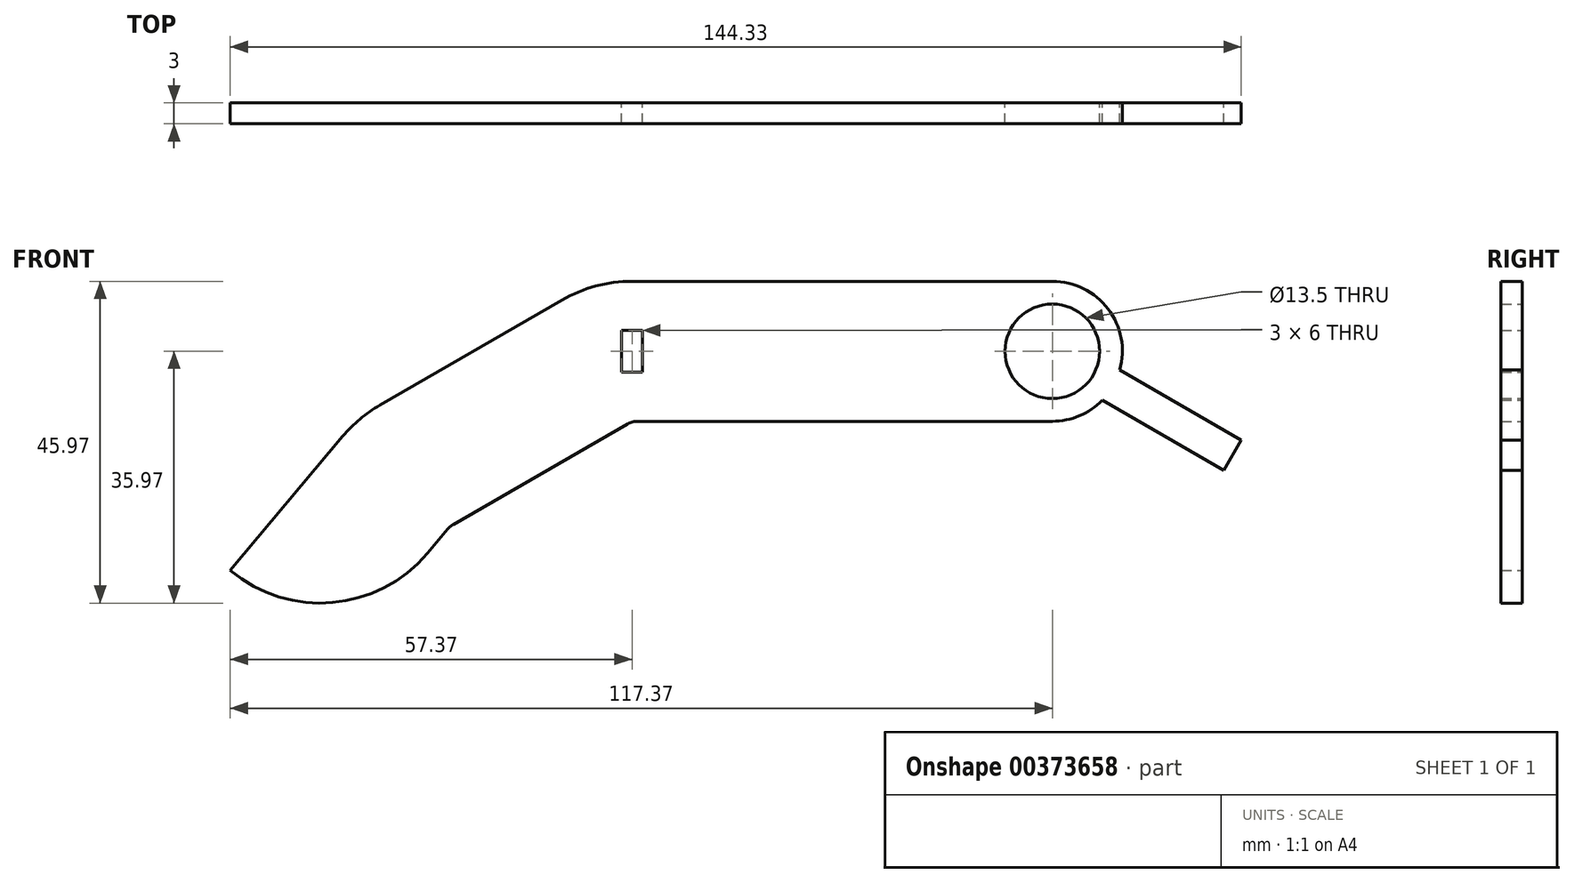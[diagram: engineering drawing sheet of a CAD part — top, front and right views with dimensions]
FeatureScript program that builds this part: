
annotation { "Feature Type Name" : "Feature", "Feature Type Description" : "" }
export const myFeature = defineFeature(function(context is Context, id is Id, definition is map)
    precondition{}
    {
        {
            var Q0;
            Q0=qCreatedBy(makeId("Front.planeOp"),FACE);
            var sketch = newSketch(context, id + "F0", { "sketchPlane" : qUnion([Q0])});
            skLineSegment(sketch, "E0.bottom", {"start": v(30, -10) * mm, "end": v(-30, -10) * mm});
            skLineSegment(sketch, "E0.top", {"start": v(30, 10) * mm, "end": v(-30, 10) * mm});
            skLineSegment(sketch, "E0.left", {"start": v(30, -10) * mm, "end": v(30, 10) * mm, "construction": true});
            skLineSegment(sketch, "E0.right", {"start": v(-30, -10) * mm, "end": v(-30, 10) * mm, "construction": true});
            skPoint(sketch, "E0.middle", {"position": v(0, 0) * mm});
            skArc(sketch, "E1", {"start": v(-30, 10) * mm, "mid": v(-35.18, 9.32) * mm, "end": v(-40, 7.32) * mm});
            skLineSegment(sketch, "E2", {"start": v(-40, 7.32) * mm, "end": v(-30, -10) * mm, "construction": true});
            skLineSegment(sketch, "E3", {"start": v(-40, 7.32) * mm, "end": v(-65.98, -7.68) * mm});
            skLineSegment(sketch, "E4", {"start": v(-30, -10) * mm, "end": v(-55.98, -25) * mm});
            skLineSegment(sketch, "E5", {"start": v(-65.98, -7.68) * mm, "end": v(-55.98, -25) * mm, "construction": true});
            skArc(sketch, "E6", {"start": v(-65.98, -7.68) * mm, "mid": v(-68.84, -9.68) * mm, "end": v(-71.3, -12.14) * mm});
            skLineSegment(sketch, "E7", {"start": v(-71.3, -12.14) * mm, "end": v(-55.98, -25) * mm, "construction": true});
            skLineSegment(sketch, "E8", {"start": v(-71.3, -12.14) * mm, "end": v(-87.37, -31.3) * mm});
            skLineSegment(sketch, "E9", {"start": v(-55.98, -25) * mm, "end": v(-59.2, -28.83) * mm});
            skArc(sketch, "E10", {"start": v(-87.37, -31.3) * mm, "mid": v(-72.77, -35.9) * mm, "end": v(-59.2, -28.83) * mm});
            skCircle(sketch, "E11", {"center": v(30, 0) * mm, "radius": 6.75 * mm});
            skLineSegment(sketch, "E12", {"start": v(30, 0) * mm, "end": v(55.7, -14.84) * mm, "construction": true});
            skArc(sketch, "E13", {"start": v(30, -10) * mm, "mid": v(33.87, -9.22) * mm, "end": v(37.14, -7) * mm});
            skArc(sketch, "E14", {"start": v(30, 10) * mm, "mid": v(37.96, 6.05) * mm, "end": v(39.64, -2.68) * mm});
            skLineSegment(sketch, "E15", {"start": v(56.96, -12.68) * mm, "end": v(54.46, -17) * mm});
            skLineSegment(sketch, "E16", {"start": v(54.46, -17) * mm, "end": v(37.14, -7) * mm});
            skLineSegment(sketch, "E17", {"start": v(56.96, -12.68) * mm, "end": v(39.64, -2.68) * mm});
            skLineSegment(sketch, "E18.bottom", {"start": v(-28.5, -3) * mm, "end": v(-31.5, -3) * mm});
            skLineSegment(sketch, "E18.top", {"start": v(-28.5, 3) * mm, "end": v(-31.5, 3) * mm});
            skLineSegment(sketch, "E18.left", {"start": v(-28.5, -3) * mm, "end": v(-28.5, 3) * mm});
            skLineSegment(sketch, "E18.right", {"start": v(-31.5, -3) * mm, "end": v(-31.5, 3) * mm});
            skPoint(sketch, "E18.middle", {"position": v(-30, 0) * mm});
            skSolve(sketch);
        }
        {
            var Q0;
            Q0 = qSketchRegion(id + "F0", true);
            extrude(context, id + "F1", {"entities" : qUnion([Q0]), "depth" : 3 * mm});
        }
        {
            var Q0;
            Q0=makeQuery(id+"F1.opExtrude","SWEPT_EDGE",EDGE,{"disambiguationData":[OSD([sQuery(id+"F0.wireOp",EDGE,"E0.bottom"),sQuery(id+"F0.wireOp",EDGE,"E4")])]});
            var Q1;
            Q1=makeQuery(id+"F1.opExtrude","SWEPT_EDGE",EDGE,{"disambiguationData":[OSD([sQuery(id+"F0.wireOp",EDGE,"E4"),sQuery(id+"F0.wireOp",EDGE,"E9")])]});
            fillet(context, id + "F2", {"entities" : qUnion([Q0, Q1]), "radius" : 3 * mm, "tangentPropagation" : true, "allowEdgeOverflow" : false});
        }
    });
